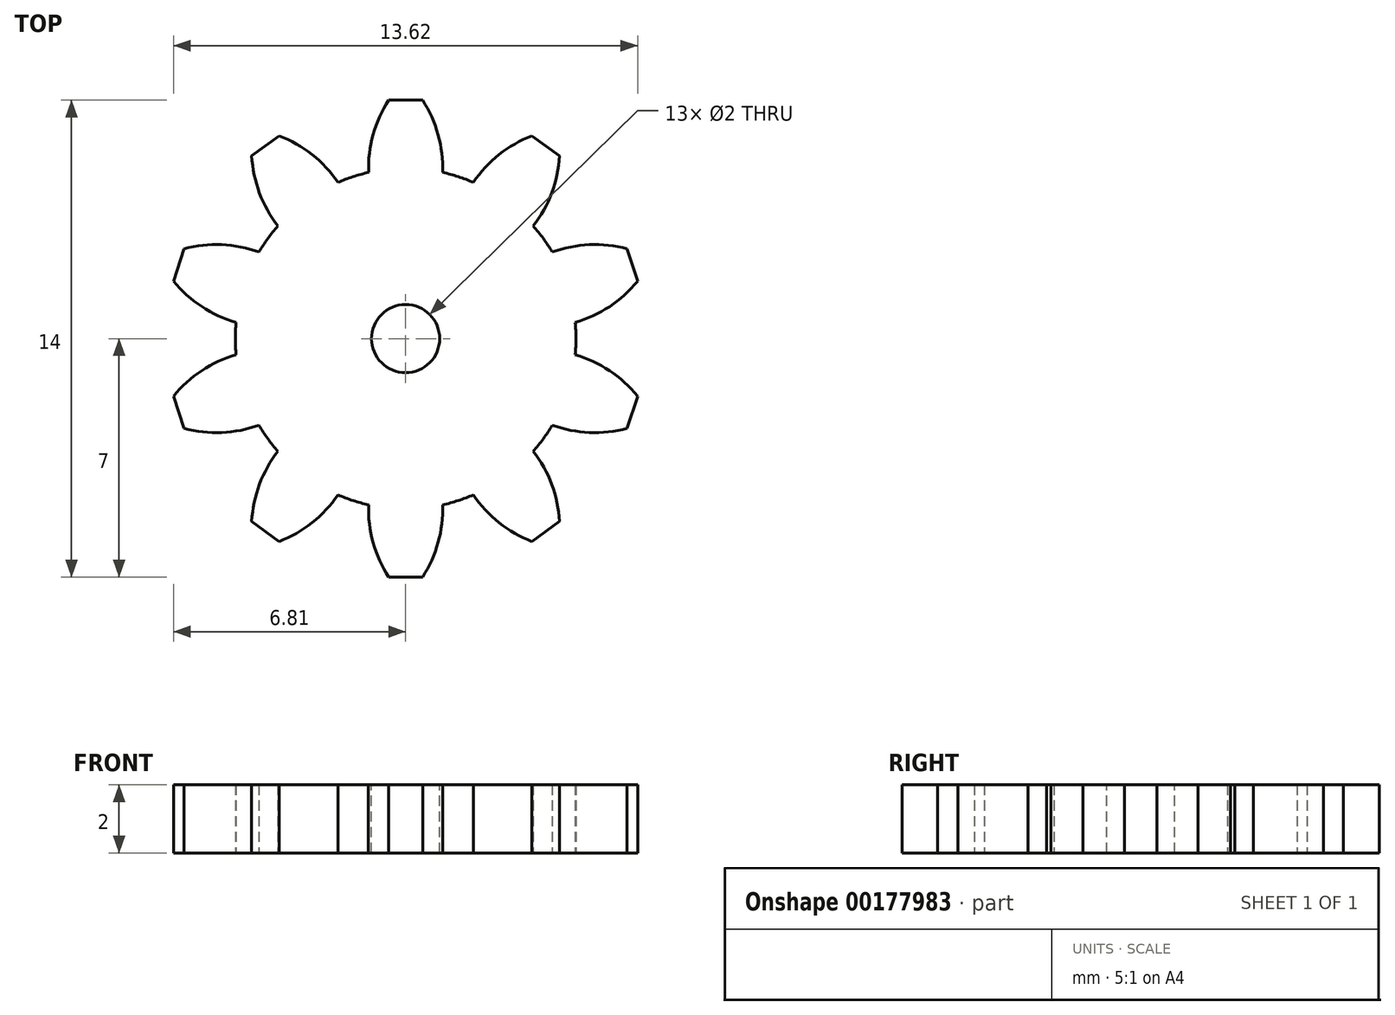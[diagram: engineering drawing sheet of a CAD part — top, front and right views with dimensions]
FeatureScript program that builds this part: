
annotation { "Feature Type Name" : "Feature", "Feature Type Description" : "" }
export const myFeature = defineFeature(function(context is Context, id is Id, definition is map)
    precondition{}
    {
        {
            var Q0;
            Q0=qCreatedBy(makeId("Top.planeOp"),FACE);
            var sketch = newSketch(context, id + "F0", { "sketchPlane" : qUnion([Q0])});
            skCircle(sketch, "E0", {"center": v(0, 0) * mm, "radius": 5 * mm});
            skLineSegment(sketch, "E1", {"start": v(0, 0) * mm, "end": v(0, 5) * mm, "construction": true});
            skArc(sketch, "E2", {"start": v(-0.5, 7) * mm, "mid": v(-0.96, 5.98) * mm, "end": v(-1.09, 4.88) * mm});
            skLineSegment(sketch, "E3", {"start": v(0, 7) * mm, "end": v(-0.5, 7) * mm});
            skLineSegment(sketch, "E4.MirrorCS", {"start": v(0, 7) * mm, "end": v(0.5, 7) * mm});
            skArc(sketch, "E5.MirrorCS", {"start": v(0.5, 7) * mm, "mid": v(0.96, 5.98) * mm, "end": v(1.09, 4.88) * mm});
            skArc(sketch, "E6.1.0", {"start": v(-3.7, 5.96) * mm, "mid": v(-2.75, 5.4) * mm, "end": v(-1.99, 4.59) * mm});
            skLineSegment(sketch, "E6.1.1", {"start": v(-4.11, 5.66) * mm, "end": v(-3.7, 5.96) * mm});
            skLineSegment(sketch, "E6.1.2", {"start": v(-4.11, 5.66) * mm, "end": v(-4.52, 5.37) * mm});
            skArc(sketch, "E6.1.3", {"start": v(-4.52, 5.37) * mm, "mid": v(-4.3, 4.28) * mm, "end": v(-3.75, 3.3) * mm});
            skArc(sketch, "E6.2.0", {"start": v(-6.5, 2.64) * mm, "mid": v(-5.4, 2.76) * mm, "end": v(-4.3, 2.54) * mm});
            skLineSegment(sketch, "E6.2.1", {"start": v(-6.66, 2.16) * mm, "end": v(-6.5, 2.64) * mm});
            skLineSegment(sketch, "E6.2.2", {"start": v(-6.66, 2.16) * mm, "end": v(-6.81, 1.69) * mm});
            skArc(sketch, "E6.2.3", {"start": v(-6.81, 1.69) * mm, "mid": v(-5.99, 0.94) * mm, "end": v(-4.98, 0.47) * mm});
            skArc(sketch, "E6.3.0", {"start": v(-6.81, -1.69) * mm, "mid": v(-5.99, -0.94) * mm, "end": v(-4.98, -0.47) * mm});
            skLineSegment(sketch, "E6.3.1", {"start": v(-6.66, -2.16) * mm, "end": v(-6.81, -1.69) * mm});
            skLineSegment(sketch, "E6.3.2", {"start": v(-6.66, -2.16) * mm, "end": v(-6.5, -2.64) * mm});
            skArc(sketch, "E6.3.3", {"start": v(-6.5, -2.64) * mm, "mid": v(-5.4, -2.76) * mm, "end": v(-4.3, -2.54) * mm});
            skArc(sketch, "E6.4.0", {"start": v(-4.52, -5.37) * mm, "mid": v(-4.3, -4.28) * mm, "end": v(-3.75, -3.3) * mm});
            skLineSegment(sketch, "E6.4.1", {"start": v(-4.11, -5.66) * mm, "end": v(-4.52, -5.37) * mm});
            skLineSegment(sketch, "E6.4.2", {"start": v(-4.11, -5.66) * mm, "end": v(-3.7, -5.96) * mm});
            skArc(sketch, "E6.4.3", {"start": v(-3.7, -5.96) * mm, "mid": v(-2.75, -5.4) * mm, "end": v(-1.99, -4.59) * mm});
            skArc(sketch, "E6.5.0", {"start": v(-0.5, -7) * mm, "mid": v(-0.96, -5.98) * mm, "end": v(-1.09, -4.88) * mm});
            skLineSegment(sketch, "E6.5.1", {"start": v(0, -7) * mm, "end": v(-0.5, -7) * mm});
            skLineSegment(sketch, "E6.5.2", {"start": v(0, -7) * mm, "end": v(0.5, -7) * mm});
            skArc(sketch, "E6.5.3", {"start": v(0.5, -7) * mm, "mid": v(0.96, -5.98) * mm, "end": v(1.09, -4.88) * mm});
            skArc(sketch, "E6.6.0", {"start": v(3.7, -5.96) * mm, "mid": v(2.75, -5.4) * mm, "end": v(1.99, -4.59) * mm});
            skLineSegment(sketch, "E6.6.1", {"start": v(4.11, -5.66) * mm, "end": v(3.7, -5.96) * mm});
            skLineSegment(sketch, "E6.6.2", {"start": v(4.11, -5.66) * mm, "end": v(4.52, -5.37) * mm});
            skArc(sketch, "E6.6.3", {"start": v(4.52, -5.37) * mm, "mid": v(4.3, -4.28) * mm, "end": v(3.75, -3.3) * mm});
            skArc(sketch, "E6.7.0", {"start": v(6.5, -2.64) * mm, "mid": v(5.4, -2.76) * mm, "end": v(4.3, -2.54) * mm});
            skLineSegment(sketch, "E6.7.1", {"start": v(6.66, -2.16) * mm, "end": v(6.5, -2.64) * mm});
            skLineSegment(sketch, "E6.7.2", {"start": v(6.66, -2.16) * mm, "end": v(6.81, -1.69) * mm});
            skArc(sketch, "E6.7.3", {"start": v(6.81, -1.69) * mm, "mid": v(5.99, -0.94) * mm, "end": v(4.98, -0.47) * mm});
            skArc(sketch, "E6.8.0", {"start": v(6.81, 1.69) * mm, "mid": v(5.99, 0.94) * mm, "end": v(4.98, 0.47) * mm});
            skLineSegment(sketch, "E6.8.1", {"start": v(6.66, 2.16) * mm, "end": v(6.81, 1.69) * mm});
            skLineSegment(sketch, "E6.8.2", {"start": v(6.66, 2.16) * mm, "end": v(6.5, 2.64) * mm});
            skArc(sketch, "E6.8.3", {"start": v(6.5, 2.64) * mm, "mid": v(5.4, 2.76) * mm, "end": v(4.3, 2.54) * mm});
            skArc(sketch, "E6.9.0", {"start": v(4.52, 5.37) * mm, "mid": v(4.3, 4.28) * mm, "end": v(3.75, 3.3) * mm});
            skLineSegment(sketch, "E6.9.1", {"start": v(4.11, 5.66) * mm, "end": v(4.52, 5.37) * mm});
            skLineSegment(sketch, "E6.9.2", {"start": v(4.11, 5.66) * mm, "end": v(3.7, 5.96) * mm});
            skArc(sketch, "E6.9.3", {"start": v(3.7, 5.96) * mm, "mid": v(2.75, 5.4) * mm, "end": v(1.99, 4.59) * mm});
            skSolve(sketch);
        }
        {
            var Q0;
            Q0=qSketchRegion(id+"F0",true);
            extrude(context, id + "F1", {"entities" : qUnion([Q0]), "depth" : 2 * mm});
        }
        {
            var Q0;
            Q0=makeQuery(id+"F1.opExtrude","CAP_FACE",FACE,{"disambiguationData":[OSD([sQuery(id+"F0.wireOp",EDGE,"E0"),sQuery(id+"F0.wireOp",EDGE,"E2"),sQuery(id+"F0.wireOp",EDGE,"E3"),sQuery(id+"F0.wireOp",EDGE,"E4.MirrorCS"),sQuery(id+"F0.wireOp",EDGE,"E5.MirrorCS"),sQuery(id+"F0.wireOp",EDGE,"E6.1.0"),sQuery(id+"F0.wireOp",EDGE,"E6.1.1"),sQuery(id+"F0.wireOp",EDGE,"E6.1.2"),sQuery(id+"F0.wireOp",EDGE,"E6.1.3"),sQuery(id+"F0.wireOp",EDGE,"E6.2.0"),sQuery(id+"F0.wireOp",EDGE,"E6.2.1"),sQuery(id+"F0.wireOp",EDGE,"E6.2.2"),sQuery(id+"F0.wireOp",EDGE,"E6.2.3"),sQuery(id+"F0.wireOp",EDGE,"E6.3.0"),sQuery(id+"F0.wireOp",EDGE,"E6.3.1"),sQuery(id+"F0.wireOp",EDGE,"E6.3.2"),sQuery(id+"F0.wireOp",EDGE,"E6.3.3"),sQuery(id+"F0.wireOp",EDGE,"E6.4.0"),sQuery(id+"F0.wireOp",EDGE,"E6.4.1"),sQuery(id+"F0.wireOp",EDGE,"E6.4.2"),sQuery(id+"F0.wireOp",EDGE,"E6.4.3"),sQuery(id+"F0.wireOp",EDGE,"E6.5.0"),sQuery(id+"F0.wireOp",EDGE,"E6.5.1"),sQuery(id+"F0.wireOp",EDGE,"E6.5.2"),sQuery(id+"F0.wireOp",EDGE,"E6.5.3"),sQuery(id+"F0.wireOp",EDGE,"E6.6.0"),sQuery(id+"F0.wireOp",EDGE,"E6.6.1"),sQuery(id+"F0.wireOp",EDGE,"E6.6.2"),sQuery(id+"F0.wireOp",EDGE,"E6.6.3"),sQuery(id+"F0.wireOp",EDGE,"E6.7.0"),sQuery(id+"F0.wireOp",EDGE,"E6.7.1"),sQuery(id+"F0.wireOp",EDGE,"E6.7.2"),sQuery(id+"F0.wireOp",EDGE,"E6.7.3"),sQuery(id+"F0.wireOp",EDGE,"E6.8.0"),sQuery(id+"F0.wireOp",EDGE,"E6.8.1"),sQuery(id+"F0.wireOp",EDGE,"E6.8.2"),sQuery(id+"F0.wireOp",EDGE,"E6.8.3"),sQuery(id+"F0.wireOp",EDGE,"E6.9.0"),sQuery(id+"F0.wireOp",EDGE,"E6.9.1"),sQuery(id+"F0.wireOp",EDGE,"E6.9.2"),sQuery(id+"F0.wireOp",EDGE,"E6.9.3"),sQuery(id+"F0.wireOp",EDGE,"E6.10.0"),sQuery(id+"F0.wireOp",EDGE,"E6.10.1"),sQuery(id+"F0.wireOp",EDGE,"E6.10.2"),sQuery(id+"F0.wireOp",EDGE,"E6.10.3"),sQuery(id+"F0.wireOp",EDGE,"E6.11.0"),sQuery(id+"F0.wireOp",EDGE,"E6.11.1"),sQuery(id+"F0.wireOp",EDGE,"E6.11.2"),sQuery(id+"F0.wireOp",EDGE,"E6.11.3"),sQuery(id+"F0.wireOp",EDGE,"E6.12.0"),sQuery(id+"F0.wireOp",EDGE,"E6.12.1"),sQuery(id+"F0.wireOp",EDGE,"E6.12.2"),sQuery(id+"F0.wireOp",EDGE,"E6.12.3"),sQuery(id+"F0.wireOp",EDGE,"E6.13.0"),sQuery(id+"F0.wireOp",EDGE,"E6.13.1"),sQuery(id+"F0.wireOp",EDGE,"E6.13.2"),sQuery(id+"F0.wireOp",EDGE,"E6.13.3"),sQuery(id+"F0.wireOp",EDGE,"E6.14.0"),sQuery(id+"F0.wireOp",EDGE,"E6.14.1"),sQuery(id+"F0.wireOp",EDGE,"E6.14.2"),sQuery(id+"F0.wireOp",EDGE,"E6.14.3"),sQuery(id+"F0.wireOp",EDGE,"E6.15.0"),sQuery(id+"F0.wireOp",EDGE,"E6.15.1"),sQuery(id+"F0.wireOp",EDGE,"E6.15.2"),sQuery(id+"F0.wireOp",EDGE,"E6.15.3")])],"isStart":false});
            var sketch = newSketch(context, id + "F2", { "sketchPlane" : qUnion([Q0])});
            skCircle(sketch, "E7", {"center": v(0, 0) * mm, "radius": 1 * mm});
            skSolve(sketch);
        }
        {
            var Q0;
            Q0=qSketchRegion(id+"F2",true);
            extrude(context, id + "F3", {"entities" : qUnion([Q0]), "operationType" : NewBodyOperationType.REMOVE, "oppositeDirection" : true, "depth" : 25 * mm});
        }
    });
